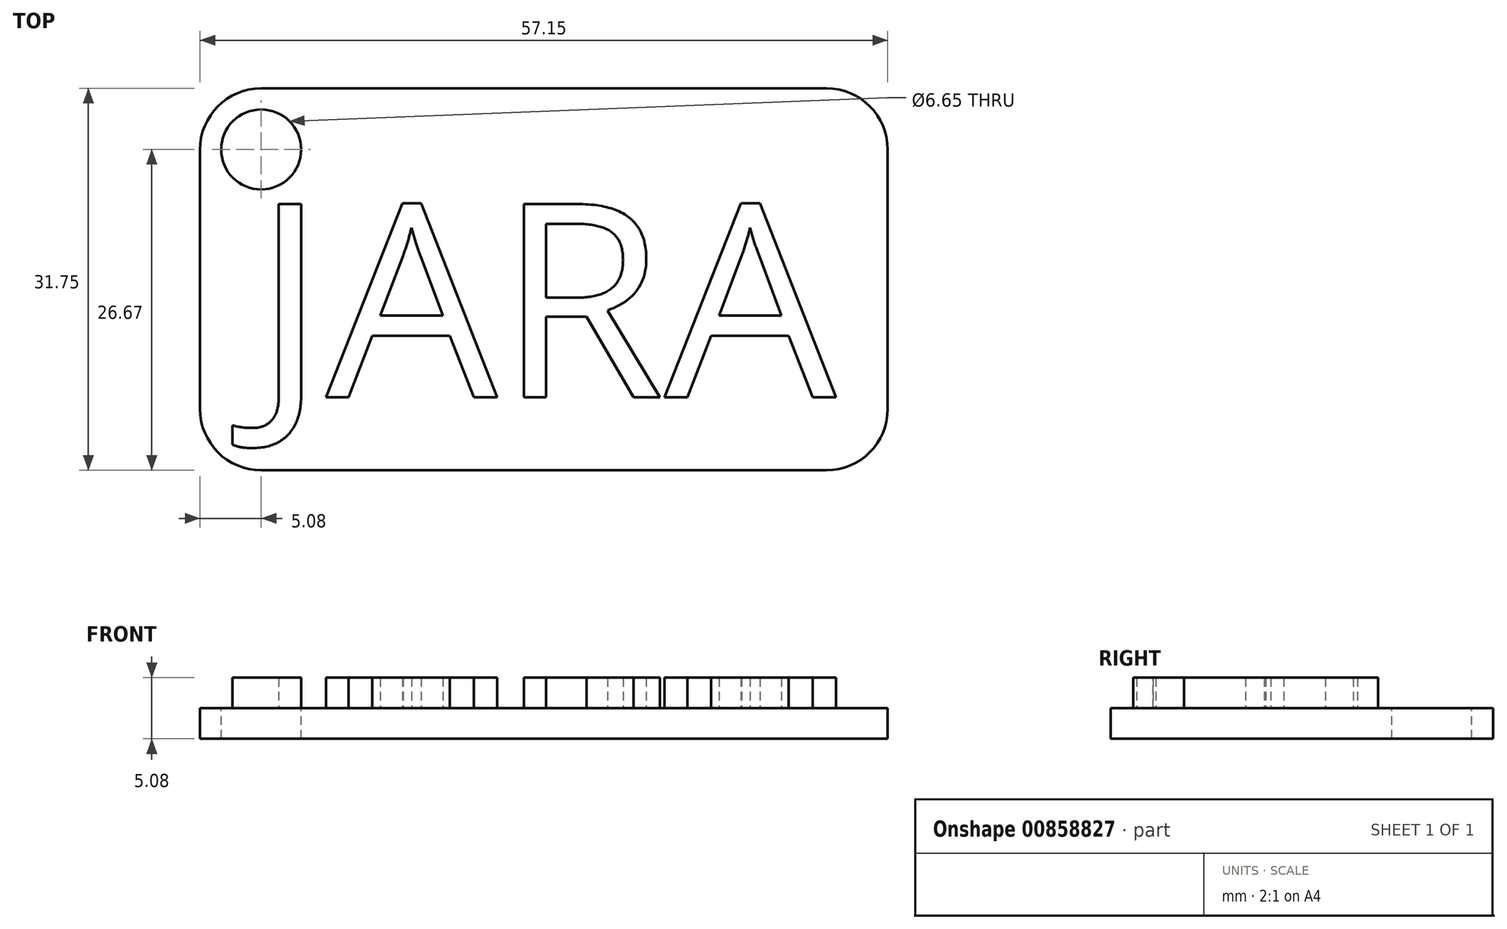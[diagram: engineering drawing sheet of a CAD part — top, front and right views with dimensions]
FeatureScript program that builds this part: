
annotation { "Feature Type Name" : "Feature", "Feature Type Description" : "" }
export const myFeature = defineFeature(function(context is Context, id is Id, definition is map)
    precondition{}
    {
        {
            var Q0;
            Q0=qCreatedBy(makeId("Top.planeOp"),FACE);
            var sketch = newSketch(context, id + "F0", { "sketchPlane" : qUnion([Q0])});
            skLineSegment(sketch, "E0.bottom", {"start": v(0, 0) * mm, "end": v(57.15, 0) * mm});
            skLineSegment(sketch, "E0.top", {"start": v(0, 31.75) * mm, "end": v(57.15, 31.75) * mm});
            skLineSegment(sketch, "E0.left", {"start": v(0, 0) * mm, "end": v(0, 31.75) * mm});
            skLineSegment(sketch, "E0.right", {"start": v(57.15, 0) * mm, "end": v(57.15, 31.75) * mm});
            skSolve(sketch);
        }
        {
            var Q0;
            Q0=makeQuery(id+"F0.imprint","IMPRINT",FACE,{"disambiguationData":[TD([[makeQuery(id+"F0.imprint","IMPRINT",EDGE,{"derivedFrom":sQuery(id+"F0.wireOp",EDGE,"E0.bottom")}),1.0]])]});
            extrude(context, id + "F1", {"entities" : qUnion([Q0]), "depth" : 2.54 * mm, "offsetDistance" : 25.4 * mm});
        }
        {
            var Q0;
            Q0=makeQuery(id+"F1.opExtrude","SWEPT_EDGE",EDGE,{"disambiguationData":[OSD([sQuery(id+"F0.wireOp",EDGE,"E0.top"),sQuery(id+"F0.wireOp",EDGE,"E0.left")])]});
            fillet(context, id + "F2", {"entities" : qUnion([Q0]), "radius" : 5.08 * mm, "tangentPropagation" : true, "allowEdgeOverflow" : false});
        }
        {
            var Q0;
            Q0=makeQuery(id+"F1.opExtrude","SWEPT_EDGE",EDGE,{"disambiguationData":[OSD([sQuery(id+"F0.wireOp",EDGE,"E0.bottom"),sQuery(id+"F0.wireOp",EDGE,"E0.left")])]});
            fillet(context, id + "F3", {"entities" : qUnion([Q0]), "radius" : 5.08 * mm, "tangentPropagation" : true, "allowEdgeOverflow" : false});
        }
        {
            var Q0;
            Q0=makeQuery(id+"F1.opExtrude","SWEPT_EDGE",EDGE,{"disambiguationData":[OSD([sQuery(id+"F0.wireOp",EDGE,"E0.top"),sQuery(id+"F0.wireOp",EDGE,"E0.right")])]});
            fillet(context, id + "F4", {"entities" : qUnion([Q0]), "radius" : 5.08 * mm, "tangentPropagation" : true, "allowEdgeOverflow" : false});
        }
        {
            var Q0;
            Q0=makeQuery(id+"F1.opExtrude","SWEPT_EDGE",EDGE,{"disambiguationData":[OSD([sQuery(id+"F0.wireOp",EDGE,"E0.bottom"),sQuery(id+"F0.wireOp",EDGE,"E0.right")])]});
            fillet(context, id + "F5", {"entities" : qUnion([Q0]), "radius" : 5.08 * mm, "tangentPropagation" : true, "allowEdgeOverflow" : false});
        }
        {
            var Q0;
            Q0=makeQuery(id+"F1.opExtrude","CAP_FACE",FACE,{"disambiguationData":[OSD([sQuery(id+"F0.wireOp",EDGE,"E0.bottom"),sQuery(id+"F0.wireOp",EDGE,"E0.top"),sQuery(id+"F0.wireOp",EDGE,"E0.left"),sQuery(id+"F0.wireOp",EDGE,"E0.right")])],"isStart":false});
            var sketch = newSketch(context, id + "F6", { "sketchPlane" : qUnion([Q0])});
            skText(sketch, "E1", { "text": "JARA", "fontName": "OpenSans-Regular.ttf"});
            const initialGuessF6  = {"E1": [0.00445, 0.00607, 1, 0, 0.0162]};
            skSetInitialGuess(sketch, initialGuessF6);
            skSolve(sketch);
        }
        {
            var Q0;
            Q0 = qSketchRegion(id + "F6", true);
            extrude(context, id + "F7", {"entities" : qUnion([Q0]), "operationType" : NewBodyOperationType.ADD, "depth" : 2.54 * mm, "offsetDistance" : 25.4 * mm});
        }
        {
            var Q0;
            {var subQ0=sQuery(id+"F0.wireOp",EDGE,"E0.left");var subQ1=sQuery(id+"F0.wireOp",EDGE,"E0.top");var subQ2=sQuery(id+"F0.wireOp",EDGE,"E0.bottom");var subQ3=sQuery(id+"F0.wireOp",EDGE,"E0.right");Q0=makeQuery(id+"F7.boolean.opBoolean","SPLIT",FACE,{"disambiguationData":[TD([makeQuery(id+"F1.opExtrude","SWEPT_FACE",FACE,{"disambiguationData":[OSD([subQ2])]})])],"derivedFrom":makeQuery(id+"F1.opExtrude","CAP_FACE",FACE,{"disambiguationData":[OSD([subQ2,subQ1,subQ0,subQ3])],"isStart":false})});}
            var sketch = newSketch(context, id + "F8", { "sketchPlane" : qUnion([Q0])});
            skCircle(sketch, "E2", {"center": v(5.08, 26.67) * mm, "radius": 3.32 * mm});
            skSolve(sketch);
        }
        {
            var Q0;
            Q0=makeQuery(id+"F8.imprint","IMPRINT",FACE,{"disambiguationData":[TD([[makeQuery(id+"F8.imprint","IMPRINT",EDGE,{"derivedFrom":sQuery(id+"F8.wireOp",EDGE,"E2")}),1.0]])]});
            extrude(context, id + "F9", {"entities" : qUnion([Q0]), "operationType" : NewBodyOperationType.REMOVE, "oppositeDirection" : true, "depth" : 25.4 * mm, "offsetDistance" : 25.4 * mm});
        }
    });
